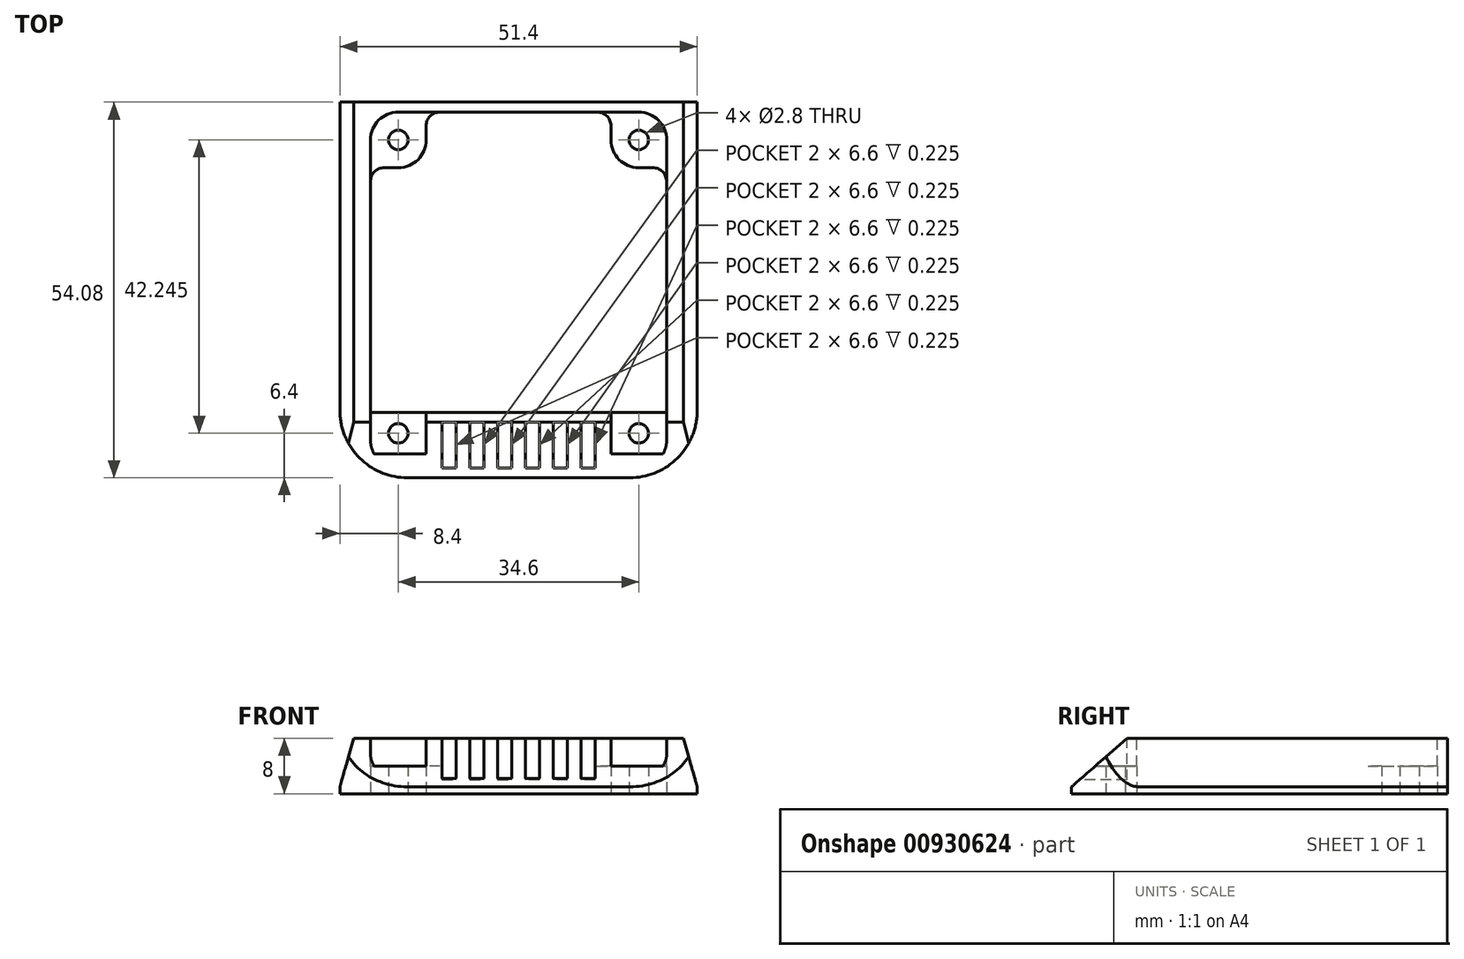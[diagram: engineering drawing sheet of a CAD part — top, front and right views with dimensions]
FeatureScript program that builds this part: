
annotation { "Feature Type Name" : "Feature", "Feature Type Description" : "" }
export const myFeature = defineFeature(function(context is Context, id is Id, definition is map)
    precondition{}
    {
        {
            var Q0;
            Q0=qCreatedBy(makeId("Top.planeOp"),FACE);
            var sketch = newSketch(context, id + "F0", { "sketchPlane" : qUnion([Q0])});
            skLineSegment(sketch, "E0", {"start": v(0, 42.65) * mm, "end": v(0, 0) * mm, "construction": true});
            skLineSegment(sketch, "E1", {"start": v(0, 42.65) * mm, "end": v(42, 42.65) * mm, "construction": true});
            skLineSegment(sketch, "E2", {"start": v(42, 42.65) * mm, "end": v(42, 0) * mm, "construction": true});
            skLineSegment(sketch, "E3", {"start": v(0, 0) * mm, "end": v(42, 0) * mm, "construction": true});
            skLineSegment(sketch, "E4", {"start": v(7.7, 42.95) * mm, "end": v(34.3, 42.95) * mm});
            skLineSegment(sketch, "E5", {"start": v(-0.3, 34.95) * mm, "end": v(-0.3, -0.3) * mm});
            skLineSegment(sketch, "E6", {"start": v(-0.3, -0.3) * mm, "end": v(42.3, -0.3) * mm});
            skLineSegment(sketch, "E7", {"start": v(42.3, 34.95) * mm, "end": v(42.3, -0.3) * mm});
            skLineSegment(sketch, "E8", {"start": v(-5, 44.68) * mm, "end": v(47, 44.68) * mm, "construction": true});
            skLineSegment(sketch, "E9", {"start": v(47, 44.68) * mm, "end": v(47, -0.02) * mm, "construction": true});
            skLineSegment(sketch, "E10", {"start": v(-5, 44.68) * mm, "end": v(-5, -0.02) * mm, "construction": true});
            skLineSegment(sketch, "E11", {"start": v(4.98, -10) * mm, "end": v(37.02, -10) * mm, "construction": true});
            skArc(sketch, "E12", {"start": v(-5, -0.02) * mm, "mid": v(-2.08, -7.08) * mm, "end": v(4.98, -10) * mm, "construction": true});
            skArc(sketch, "E13", {"start": v(37.02, -10) * mm, "mid": v(44.08, -7.08) * mm, "end": v(47, -0.02) * mm, "construction": true});
            skLineSegment(sketch, "E14", {"start": v(-4.7, 44.38) * mm, "end": v(-4.7, -0.02) * mm});
            skLineSegment(sketch, "E15", {"start": v(-4.7, 44.38) * mm, "end": v(46.7, 44.38) * mm});
            skLineSegment(sketch, "E16", {"start": v(46.7, 44.38) * mm, "end": v(46.7, -0.02) * mm});
            skLineSegment(sketch, "E17", {"start": v(4.98, -9.7) * mm, "end": v(37.02, -9.7) * mm});
            skArc(sketch, "E18", {"start": v(-4.7, -0.02) * mm, "mid": v(-1.87, -6.87) * mm, "end": v(4.98, -9.7) * mm});
            skArc(sketch, "E19", {"start": v(37.02, -9.7) * mm, "mid": v(43.87, -6.87) * mm, "end": v(46.7, -0.02) * mm});
            skLineSegment(sketch, "E20", {"start": v(-0.3, 34.95) * mm, "end": v(3.7, 34.95) * mm});
            skLineSegment(sketch, "E21", {"start": v(7.7, 42.95) * mm, "end": v(7.7, 38.95) * mm});
            skArc(sketch, "E22", {"start": v(3.7, 34.95) * mm, "mid": v(6.53, 36.12) * mm, "end": v(7.7, 38.95) * mm});
            skCircle(sketch, "E23", {"center": v(3.7, 38.95) * mm, "radius": 1.4 * mm});
            skLineSegment(sketch, "E24", {"start": v(34.3, 42.95) * mm, "end": v(34.3, 38.95) * mm});
            skLineSegment(sketch, "E25", {"start": v(42.3, 34.95) * mm, "end": v(38.3, 34.95) * mm});
            skArc(sketch, "E26", {"start": v(34.3, 38.95) * mm, "mid": v(35.47, 36.12) * mm, "end": v(38.3, 34.95) * mm});
            skCircle(sketch, "E27", {"center": v(38.3, 38.95) * mm, "radius": 1.4 * mm});
            skSolve(sketch);
        }
        {
            var Q0;
            Q0=qSketchRegion(id+"F0",true);
            extrude(context, id + "F1", {"entities" : qUnion([Q0]), "depth" : 8 * mm, "offsetDistance" : 25 * mm});
        }
        {
            var Q0;
            Q0=makeQuery(id+"F1.opExtrude","SWEPT_FACE",FACE,{"disambiguationData":[OSD([sQuery(id+"F0.wireOp",EDGE,"E15")])]});
            var sketch = newSketch(context, id + "F2", { "sketchPlane" : qUnion([Q0])});
            skLineSegment(sketch, "E28", {"start": v(4.7, 8) * mm, "end": v(2.7, 8) * mm});
            skLineSegment(sketch, "E29", {"start": v(2.7, 8) * mm, "end": v(4.7, 1) * mm});
            skLineSegment(sketch, "E30", {"start": v(4.7, 1) * mm, "end": v(4.7, 8) * mm});
            skLineSegment(sketch, "E31", {"start": v(-46.7, 8) * mm, "end": v(-46.7, 1) * mm});
            skLineSegment(sketch, "E32", {"start": v(-46.7, 1) * mm, "end": v(-44.7, 8) * mm});
            skLineSegment(sketch, "E33", {"start": v(-44.7, 8) * mm, "end": v(-46.7, 8) * mm});
            skSolve(sketch);
        }
        {
            var Q0;
            Q0=qSketchRegion(id+"F2",true);
            extrude(context, id + "F3", {"entities" : qUnion([Q0]), "operationType" : NewBodyOperationType.REMOVE, "endBound" : BoundingType.THROUGH_ALL, "oppositeDirection" : true, "depth" : 25 * mm, "offsetDistance" : 25 * mm});
        }
        {
            var Q0;
            Q0=makeQuery(id+"F1.opExtrude","SWEPT_FACE",FACE,{"disambiguationData":[OSD([sQuery(id+"F0.wireOp",EDGE,"E14")])]});
            var sketch = newSketch(context, id + "F4", { "sketchPlane" : qUnion([Q0])});
            skLineSegment(sketch, "E34", {"start": v(1.7, 8) * mm, "end": v(9.7, 1) * mm});
            skLineSegment(sketch, "E35", {"start": v(9.7, 1) * mm, "end": v(9.7, 8) * mm});
            skLineSegment(sketch, "E36", {"start": v(9.7, 8) * mm, "end": v(1.7, 8) * mm});
            skSolve(sketch);
        }
        {
            var Q0;
            Q0=qSketchRegion(id+"F4",true);
            extrude(context, id + "F5", {"entities" : qUnion([Q0]), "operationType" : NewBodyOperationType.REMOVE, "endBound" : BoundingType.THROUGH_ALL, "oppositeDirection" : true, "depth" : 25 * mm, "offsetDistance" : 25 * mm});
        }
        {
            var Q0;
            Q0=makeQuery(id+"F1.opExtrude","SWEPT_EDGE",EDGE,{"disambiguationData":[OSD([sQuery(id+"F0.wireOp",EDGE,"E4"),sQuery(id+"F0.wireOp",EDGE,"E21")])]});
            var Q1;
            Q1=makeQuery(id+"F1.opExtrude","SWEPT_EDGE",EDGE,{"disambiguationData":[OSD([sQuery(id+"F0.wireOp",EDGE,"E4"),sQuery(id+"F0.wireOp",EDGE,"E24")])]});
            var Q2;
            Q2=makeQuery(id+"F1.opExtrude","SWEPT_EDGE",EDGE,{"disambiguationData":[OSD([sQuery(id+"F0.wireOp",EDGE,"E7"),sQuery(id+"F0.wireOp",EDGE,"E25")])]});
            var Q3;
            Q3=makeQuery(id+"F1.opExtrude","SWEPT_EDGE",EDGE,{"disambiguationData":[OSD([sQuery(id+"F0.wireOp",EDGE,"E5"),sQuery(id+"F0.wireOp",EDGE,"E20")])]});
            fillet(context, id + "F6", {"entities" : qUnion([Q0, Q1, Q2, Q3]), "radius" : 2 * mm, "tangentPropagation" : true, "allowEdgeOverflow" : false});
        }
        {
            var Q0;
            Q0=makeQuery(id+"F1.opExtrude","CAP_FACE",FACE,{"disambiguationData":[OSD([sQuery(id+"F0.wireOp",EDGE,"E4"),sQuery(id+"F0.wireOp",EDGE,"E5"),sQuery(id+"F0.wireOp",EDGE,"E6"),sQuery(id+"F0.wireOp",EDGE,"E7"),sQuery(id+"F0.wireOp",EDGE,"E14"),sQuery(id+"F0.wireOp",EDGE,"E15"),sQuery(id+"F0.wireOp",EDGE,"E16"),sQuery(id+"F0.wireOp",EDGE,"E17"),sQuery(id+"F0.wireOp",EDGE,"E18"),sQuery(id+"F0.wireOp",EDGE,"E19"),sQuery(id+"F0.wireOp",EDGE,"E20"),sQuery(id+"F0.wireOp",EDGE,"E21"),sQuery(id+"F0.wireOp",EDGE,"E22"),sQuery(id+"F0.wireOp",EDGE,"E23"),sQuery(id+"F0.wireOp",EDGE,"E24"),sQuery(id+"F0.wireOp",EDGE,"E25"),sQuery(id+"F0.wireOp",EDGE,"E26"),sQuery(id+"F0.wireOp",EDGE,"E27")])],"isStart":false});
            var sketch = newSketch(context, id + "F7", { "sketchPlane" : qUnion([Q0])});
            skArc(sketch, "E37", {"start": v(3.7, 42.95) * mm, "mid": v(0.87, 41.77) * mm, "end": v(-0.3, 38.95) * mm});
            skLineSegment(sketch, "E38", {"start": v(9.7, 42.95) * mm, "end": v(3.7, 42.95) * mm});
            skLineSegment(sketch, "E39", {"start": v(-0.3, 32.95) * mm, "end": v(-0.3, 38.95) * mm});
            skLineSegment(sketch, "E40", {"start": v(32.3, 42.95) * mm, "end": v(38.3, 42.95) * mm});
            skLineSegment(sketch, "E41", {"start": v(42.3, 32.95) * mm, "end": v(42.3, 38.95) * mm});
            skArc(sketch, "E42", {"start": v(42.3, 38.95) * mm, "mid": v(41.13, 41.77) * mm, "end": v(38.3, 42.95) * mm});
            skArc(sketch, "E43", {"start": v(9.7, 42.95) * mm, "mid": v(8.29, 42.36) * mm, "end": v(7.7, 40.95) * mm});
            skArc(sketch, "E44", {"start": v(1.7, 34.95) * mm, "mid": v(0.29, 34.36) * mm, "end": v(-0.3, 32.95) * mm});
            skArc(sketch, "E45", {"start": v(3.7, 34.95) * mm, "mid": v(6.53, 36.12) * mm, "end": v(7.7, 38.95) * mm});
            skArc(sketch, "E46", {"start": v(34.3, 40.95) * mm, "mid": v(33.71, 42.36) * mm, "end": v(32.3, 42.95) * mm});
            skArc(sketch, "E47", {"start": v(42.3, 32.95) * mm, "mid": v(41.71, 34.36) * mm, "end": v(40.3, 34.95) * mm});
            skArc(sketch, "E48", {"start": v(34.3, 38.95) * mm, "mid": v(35.47, 36.12) * mm, "end": v(38.3, 34.95) * mm});
            skLineSegment(sketch, "E49", {"start": v(3.7, 34.95) * mm, "end": v(1.7, 34.95) * mm});
            skLineSegment(sketch, "E50", {"start": v(7.7, 38.95) * mm, "end": v(7.7, 40.95) * mm});
            skLineSegment(sketch, "E51", {"start": v(34.3, 40.95) * mm, "end": v(34.3, 38.95) * mm});
            skLineSegment(sketch, "E52", {"start": v(38.3, 34.95) * mm, "end": v(40.3, 34.95) * mm});
            skLineSegment(sketch, "E53", {"start": v(-0.3, -0.3) * mm, "end": v(-0.3, -4.3) * mm});
            skLineSegment(sketch, "E54", {"start": v(7.7, -0.3) * mm, "end": v(7.7, -8.3) * mm});
            skLineSegment(sketch, "E55", {"start": v(-0.3, -0.3) * mm, "end": v(7.7, -0.3) * mm});
            skLineSegment(sketch, "E56", {"start": v(7.7, -8.3) * mm, "end": v(3.7, -8.3) * mm});
            skLineSegment(sketch, "E57", {"start": v(42.3, -0.3) * mm, "end": v(34.3, -0.3) * mm});
            skLineSegment(sketch, "E58", {"start": v(34.3, -0.3) * mm, "end": v(34.3, -8.3) * mm});
            skLineSegment(sketch, "E59", {"start": v(34.3, -8.3) * mm, "end": v(38.3, -8.3) * mm});
            skLineSegment(sketch, "E60", {"start": v(42.3, -4.3) * mm, "end": v(42.3, -0.3) * mm});
            skPoint(sketch, "E61.visualSharp", {"position": v(-0.3, -8.3) * mm});
            skArc(sketch, "E61.filletArc", {"start": v(-0.3, -4.3) * mm, "mid": v(0.87, -7.13) * mm, "end": v(3.7, -8.3) * mm});
            skPoint(sketch, "E62.visualSharp", {"position": v(42.3, -8.3) * mm});
            skArc(sketch, "E62.filletArc", {"start": v(38.3, -8.3) * mm, "mid": v(41.13, -7.13) * mm, "end": v(42.3, -4.3) * mm});
            skLineSegment(sketch, "E63", {"start": v(21, -0.3) * mm, "end": v(21, -9.7) * mm, "construction": true});
            skSolve(sketch);
        }
        {
            var Q0;
            Q0=qSketchRegion(id+"F7",true);
            extrude(context, id + "F8", {"entities" : qUnion([Q0]), "operationType" : NewBodyOperationType.REMOVE, "oppositeDirection" : true, "depth" : 4 * mm, "offsetDistance" : 25 * mm});
        }
        {
            var Q0;
            Q0=makeQuery(id+"F8.boolean.opBoolean","COPY",FACE,{"derivedFrom":makeQuery(id+"F8.opExtrude","CAP_FACE",FACE,{"disambiguationData":[OSD([sQuery(id+"F7.wireOp",EDGE,"E53"),sQuery(id+"F7.wireOp",EDGE,"E54"),sQuery(id+"F7.wireOp",EDGE,"E55"),sQuery(id+"F7.wireOp",EDGE,"E56"),sQuery(id+"F7.wireOp",EDGE,"E61.filletArc")])],"isStart":false})});
            var sketch = newSketch(context, id + "F9", { "sketchPlane" : qUnion([Q0])});
            skCircle(sketch, "E64", {"center": v(3.7, -3.3) * mm, "radius": 1.4 * mm});
            skCircle(sketch, "E65", {"center": v(38.3, -3.3) * mm, "radius": 1.4 * mm});
            skSolve(sketch);
        }
        {
            var Q0;
            Q0=qSketchRegion(id+"F9",true);
            extrude(context, id + "F10", {"entities" : qUnion([Q0]), "operationType" : NewBodyOperationType.REMOVE, "endBound" : BoundingType.UP_TO_NEXT, "oppositeDirection" : true, "depth" : 25 * mm, "offsetDistance" : 25 * mm});
        }
        {
            var Q0;
            {var subQ0=sQuery(id+"F0.wireOp",EDGE,"E6");Q0=makeQuery(id+"F8.boolean.opBoolean","SPLIT",FACE,{"disambiguationData":[TD([makeQuery(id+"F1.opExtrude","SWEPT_FACE",FACE,{"disambiguationData":[OSD([subQ0])]})])],"derivedFrom":makeQuery(id+"F1.opExtrude","CAP_FACE",FACE,{"disambiguationData":[OSD([sQuery(id+"F0.wireOp",EDGE,"E4"),sQuery(id+"F0.wireOp",EDGE,"E5"),subQ0,sQuery(id+"F0.wireOp",EDGE,"E7"),sQuery(id+"F0.wireOp",EDGE,"E14"),sQuery(id+"F0.wireOp",EDGE,"E15"),sQuery(id+"F0.wireOp",EDGE,"E16"),sQuery(id+"F0.wireOp",EDGE,"E17"),sQuery(id+"F0.wireOp",EDGE,"E18"),sQuery(id+"F0.wireOp",EDGE,"E19"),sQuery(id+"F0.wireOp",EDGE,"E20"),sQuery(id+"F0.wireOp",EDGE,"E21"),sQuery(id+"F0.wireOp",EDGE,"E22"),sQuery(id+"F0.wireOp",EDGE,"E23"),sQuery(id+"F0.wireOp",EDGE,"E24"),sQuery(id+"F0.wireOp",EDGE,"E25"),sQuery(id+"F0.wireOp",EDGE,"E26"),sQuery(id+"F0.wireOp",EDGE,"E27")])],"isStart":false})});}
            var sketch = newSketch(context, id + "F11", { "sketchPlane" : qUnion([Q0])});
            skLineSegment(sketch, "E66", {"start": v(21, -0.3) * mm, "end": v(21, -9.7) * mm, "construction": true});
            skLineSegment(sketch, "E67.top", {"start": v(10, -8.3) * mm, "end": v(12, -8.3) * mm});
            skLineSegment(sketch, "E67.left", {"start": v(10, -1.7) * mm, "end": v(10, -8.3) * mm});
            skLineSegment(sketch, "E67.right", {"start": v(12, -1.7) * mm, "end": v(12, -8.3) * mm});
            skLineSegment(sketch, "E68.top", {"start": v(14, -8.3) * mm, "end": v(16, -8.3) * mm});
            skLineSegment(sketch, "E68.left", {"start": v(14, -1.7) * mm, "end": v(14, -8.3) * mm});
            skLineSegment(sketch, "E68.right", {"start": v(16, -1.7) * mm, "end": v(16, -8.3) * mm});
            skLineSegment(sketch, "E69.top", {"start": v(18, -8.3) * mm, "end": v(20, -8.3) * mm});
            skLineSegment(sketch, "E69.left", {"start": v(18, -1.7) * mm, "end": v(18, -8.3) * mm});
            skLineSegment(sketch, "E69.right", {"start": v(20, -1.7) * mm, "end": v(20, -8.3) * mm});
            skLineSegment(sketch, "E70.MirrorCS", {"start": v(30, -1.7) * mm, "end": v(30, -8.3) * mm});
            skLineSegment(sketch, "E71.MirrorCS", {"start": v(28, -1.7) * mm, "end": v(28, -8.3) * mm});
            skLineSegment(sketch, "E72.MirrorCS", {"start": v(24, -1.7) * mm, "end": v(24, -8.3) * mm});
            skLineSegment(sketch, "E73.MirrorCS", {"start": v(32, -8.3) * mm, "end": v(30, -8.3) * mm});
            skLineSegment(sketch, "E74.MirrorCS", {"start": v(26, -1.7) * mm, "end": v(26, -8.3) * mm});
            skLineSegment(sketch, "E75.MirrorCS", {"start": v(24, -8.3) * mm, "end": v(22, -8.3) * mm});
            skLineSegment(sketch, "E76.MirrorCS", {"start": v(28, -8.3) * mm, "end": v(26, -8.3) * mm});
            skLineSegment(sketch, "E77.MirrorCS", {"start": v(32, -1.7) * mm, "end": v(32, -8.3) * mm});
            skLineSegment(sketch, "E78.MirrorCS", {"start": v(22, -1.7) * mm, "end": v(22, -8.3) * mm});
            skLineSegment(sketch, "E79", {"start": v(10, -1.7) * mm, "end": v(12, -1.7) * mm});
            skLineSegment(sketch, "E80", {"start": v(14, -1.7) * mm, "end": v(16, -1.7) * mm});
            skLineSegment(sketch, "E81", {"start": v(18, -1.7) * mm, "end": v(20, -1.7) * mm});
            skLineSegment(sketch, "E82", {"start": v(22, -1.7) * mm, "end": v(24, -1.7) * mm});
            skLineSegment(sketch, "E83", {"start": v(26, -1.7) * mm, "end": v(28, -1.7) * mm});
            skLineSegment(sketch, "E84", {"start": v(30, -1.7) * mm, "end": v(32, -1.7) * mm});
            skSolve(sketch);
        }
        {
            var Q0;
            Q0=qSketchRegion(id+"F11",true);
            extrude(context, id + "F12", {"entities" : qUnion([Q0]), "operationType" : NewBodyOperationType.REMOVE, "oppositeDirection" : true, "depth" : 6 * mm, "offsetDistance" : 25 * mm});
        }
    });
